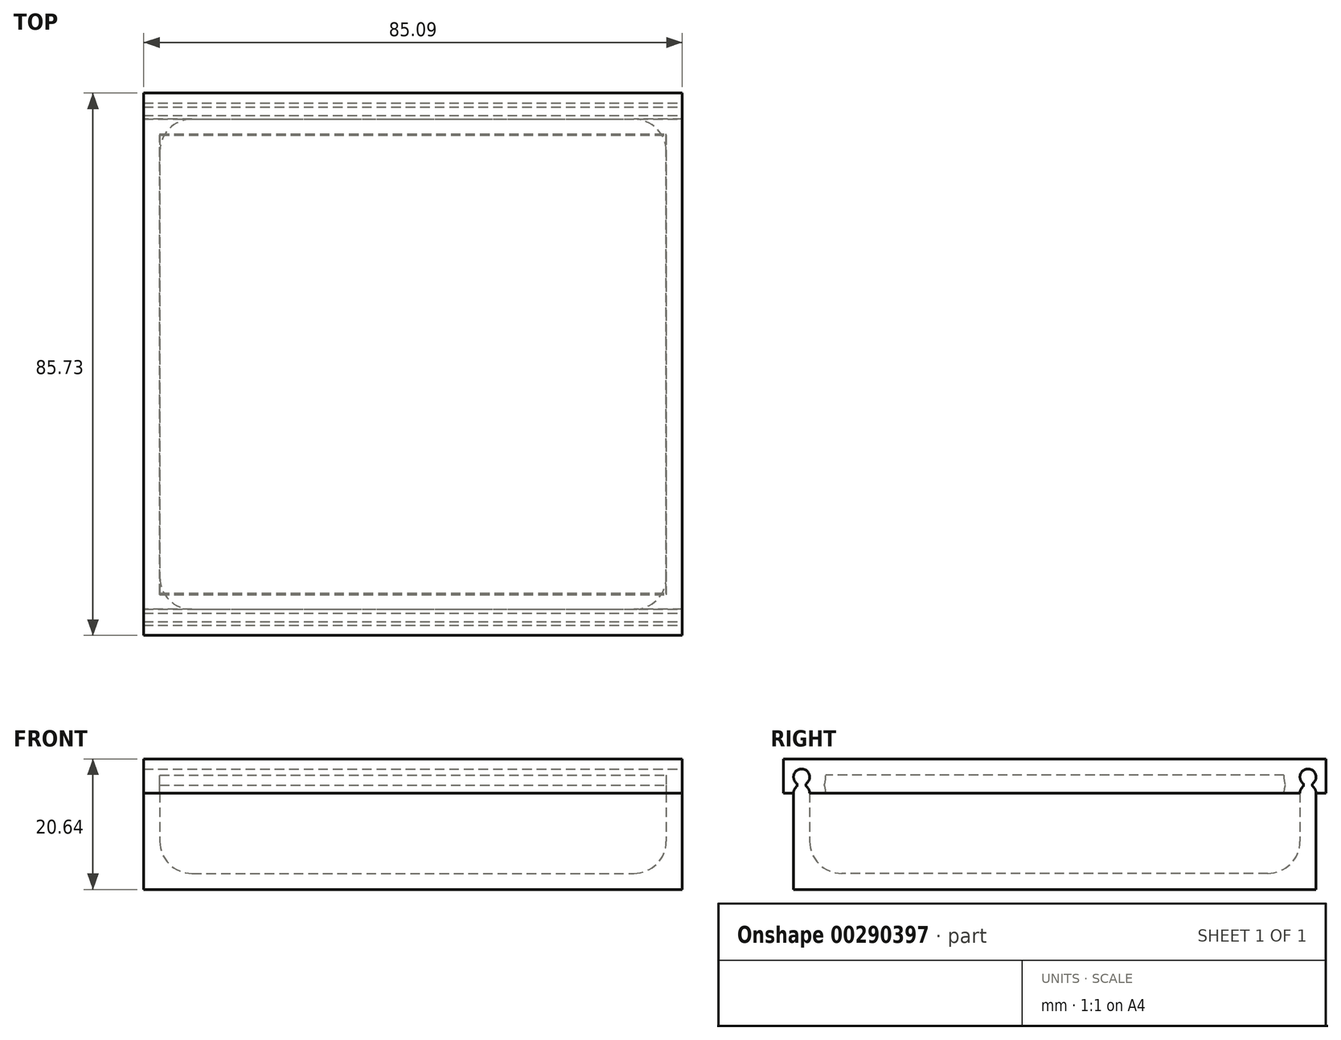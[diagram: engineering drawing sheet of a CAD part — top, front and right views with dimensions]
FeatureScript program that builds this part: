
annotation { "Feature Type Name" : "Feature", "Feature Type Description" : "" }
export const myFeature = defineFeature(function(context is Context, id is Id, definition is map)
    precondition{}
    {
        {
            var Q0;
            Q0=qCreatedBy(makeId("Top.planeOp"),FACE);
            var sketch = newSketch(context, id + "F0", { "sketchPlane" : qUnion([Q0])});
            skLineSegment(sketch, "E0.bottom", {"start": v(0, 82.55) * mm, "end": v(85.1, 82.55) * mm});
            skLineSegment(sketch, "E0.top", {"start": v(0, 0) * mm, "end": v(85.1, 0) * mm});
            skLineSegment(sketch, "E0.left", {"start": v(0, 82.55) * mm, "end": v(0, 0) * mm});
            skLineSegment(sketch, "E0.right", {"start": v(85.1, 82.55) * mm, "end": v(85.1, 0) * mm});
            skSolve(sketch);
        }
        {
            var Q0;
            Q0 = qSketchRegion(id + "F0", true);
            extrude(context, id + "F1", {"entities" : qUnion([Q0]), "depth" : 15.24 * mm, "offsetDistance" : 25.4 * mm});
        }
        {
            var Q0;
            Q0=makeQuery(id+"F1.opExtrude","CAP_FACE",FACE,{"disambiguationData":[OSD([sQuery(id+"F0.wireOp",EDGE,"E0.bottom"),sQuery(id+"F0.wireOp",EDGE,"E0.top"),sQuery(id+"F0.wireOp",EDGE,"E0.left"),sQuery(id+"F0.wireOp",EDGE,"E0.right")])],"isStart":false});
            shell(context, id + "F2", {"entities" : qUnion([Q0]), "thickness" : 2.54 * mm});
        }
        {
            var Q0;
            Q0=makeQuery(id+"F1.opExtrude","SWEPT_FACE",FACE,{"disambiguationData":[OSD([sQuery(id+"F0.wireOp",EDGE,"E0.left")])]});
            var sketch = newSketch(context, id + "F3", { "sketchPlane" : qUnion([Q0])});
            skLineSegment(sketch, "E1.bottom", {"start": v(0, 15.24) * mm, "end": v(-2.54, 15.24) * mm});
            skLineSegment(sketch, "E1.top", {"start": v(-1.27, 16.5) * mm, "end": v(-1.27, 16.5) * mm});
            skArc(sketch, "E2", {"start": v(-0.44, 16.81) * mm, "mid": v(-1.27, 19.05) * mm, "end": v(-2.1, 16.81) * mm});
            skPoint(sketch, "E2.centerSnap0", {"position": v(-1.27, 16.5) * mm});
            skPoint(sketch, "E3.visualSharp", {"position": v(-2.54, 16.5) * mm});
            skArc(sketch, "E3.filletArc", {"start": v(-2.1, 16.2) * mm, "mid": v(-2.42, 15.77) * mm, "end": v(-2.54, 15.24) * mm});
            skPoint(sketch, "E4.visualSharp", {"position": v(0, 16.5) * mm});
            skArc(sketch, "E4.filletArc", {"start": v(0, 15.24) * mm, "mid": v(-0.12, 15.77) * mm, "end": v(-0.44, 16.2) * mm});
            skArc(sketch, "E5", {"start": v(-2.1, 16.2) * mm, "mid": v(-1.95, 16.5) * mm, "end": v(-2.1, 16.81) * mm});
            skLineSegment(sketch, "E6", {"start": v(-1.27, 17.78) * mm, "end": v(-1.27, 16.5) * mm, "construction": true});
            skArc(sketch, "E7.MirrorCS", {"start": v(-0.44, 16.2) * mm, "mid": v(-0.59, 16.5) * mm, "end": v(-0.44, 16.81) * mm});
            skArc(sketch, "E8.MirrorCS", {"start": v(-0.44, 16.2) * mm, "mid": v(-0.12, 15.77) * mm, "end": v(0, 15.24) * mm});
            skLineSegment(sketch, "E9", {"start": v(-41.28, 15.24) * mm, "end": v(-41.28, 0) * mm, "construction": true});
            skArc(sketch, "E10.MirrorCS", {"start": v(-82.1, 16.2) * mm, "mid": v(-81.96, 16.5) * mm, "end": v(-82.1, 16.81) * mm});
            skArc(sketch, "E11.MirrorCS", {"start": v(-82.55, 15.24) * mm, "mid": v(-82.43, 15.77) * mm, "end": v(-82.1, 16.2) * mm});
            skArc(sketch, "E12.MirrorCS", {"start": v(-82.1, 16.2) * mm, "mid": v(-82.43, 15.77) * mm, "end": v(-82.55, 15.24) * mm});
            skArc(sketch, "E13.MirrorCS", {"start": v(-80.45, 16.2) * mm, "mid": v(-80.6, 16.5) * mm, "end": v(-80.45, 16.81) * mm});
            skLineSegment(sketch, "E14.MirrorCS", {"start": v(-82.55, 15.24) * mm, "end": v(-80.01, 15.24) * mm});
            skLineSegment(sketch, "E15.MirrorCS", {"start": v(-81.28, 17.78) * mm, "end": v(-81.28, 16.5) * mm, "construction": true});
            skArc(sketch, "E16.MirrorCS", {"start": v(-80.45, 16.2) * mm, "mid": v(-80.13, 15.77) * mm, "end": v(-80.01, 15.24) * mm});
            skPoint(sketch, "E17.MirrorP", {"position": v(-81.28, 16.5) * mm});
            skLineSegment(sketch, "E18.MirrorCS", {"start": v(-81.28, 16.5) * mm, "end": v(-81.28, 16.5) * mm});
            skPoint(sketch, "E19.MirrorP", {"position": v(-80.01, 16.5) * mm});
            skPoint(sketch, "E20.MirrorP", {"position": v(-82.55, 16.5) * mm});
            skArc(sketch, "E21.MirrorCS", {"start": v(-82.1, 16.81) * mm, "mid": v(-81.28, 19.05) * mm, "end": v(-80.45, 16.81) * mm});
            skSolve(sketch);
        }
        {
            var Q0;
            Q0 = qSketchRegion(id + "F3", true);
            var Q1;
            Q1=makeQuery(id+"F1.opExtrude","SWEPT_FACE",FACE,{"disambiguationData":[OSD([sQuery(id+"F0.wireOp",EDGE,"E0.right")])]});
            extrude(context, id + "F4", {"entities" : qUnion([Q0]), "operationType" : NewBodyOperationType.ADD, "endBound" : BoundingType.UP_TO_SURFACE, "oppositeDirection" : true, "depth" : 25.4 * mm, "endBoundEntityFace" : qUnion([Q1]), "offsetDistance" : 25.4 * mm});
        }
        {
            var Q0;
            Q0=qCreatedBy(makeId("Front.planeOp"),FACE);
            cPlane(context, id + "F5", {"entities" : qUnion([Q0]), "cplaneType" : CPlaneType.OFFSET, "offset" : 41.27 * mm, "oppositeDirection" : true, "width" : 152.4 * mm, "height" : 152.4 * mm});
        }
        {
            var Q0;
            {var subQ0=sQuery(id+"F0.wireOp",EDGE,"E0.right");Q0=makeQuery(id+"F4.boolean.opBoolean","MERGE",FACE,{"derivedFrom":[makeQuery(id+"F1.opExtrude","SWEPT_FACE",FACE,{"disambiguationData":[OSD([subQ0])]}),makeQuery(id+"F4.opExtrude","CAP_FACE",FACE,{"disambiguationData":[OSD([subQ0]),OD(0.0)],"isStart":false}),makeQuery(id+"F4.opExtrude","CAP_FACE",FACE,{"disambiguationData":[OSD([subQ0]),OD(1.0)],"isStart":false})]});}
            var sketch = newSketch(context, id + "F6", { "sketchPlane" : qUnion([Q0])});
            skLineSegment(sketch, "E22", {"start": v(2.54, 15.24) * mm, "end": v(-2.32, 15.24) * mm, "construction": true});
            skArc(sketch, "E23", {"start": v(2.54, 15.24) * mm, "mid": v(2.42, 15.77) * mm, "end": v(2.1, 16.2) * mm});
            skArc(sketch, "E24", {"start": v(2.1, 16.81) * mm, "mid": v(1.27, 19.05) * mm, "end": v(0.44, 16.81) * mm});
            skArc(sketch, "E25", {"start": v(2.1, 16.81) * mm, "mid": v(1.95, 16.5) * mm, "end": v(2.1, 16.2) * mm});
            skArc(sketch, "E26", {"start": v(0.44, 16.81) * mm, "mid": v(0.59, 16.5) * mm, "end": v(0.44, 16.2) * mm});
            skArc(sketch, "E27.trimOffspring", {"start": v(0.44, 16.2) * mm, "mid": v(0.12, 15.77) * mm, "end": v(0, 15.24) * mm});
            skLineSegment(sketch, "E28", {"start": v(0, 15.24) * mm, "end": v(-1.59, 15.24) * mm});
            skLineSegment(sketch, "E29", {"start": v(-1.59, 15.24) * mm, "end": v(-1.59, 20.64) * mm});
            skLineSegment(sketch, "E30", {"start": v(1.27, 19.05) * mm, "end": v(-1.87, 19.05) * mm, "construction": true});
            skArc(sketch, "E31.MirrorCS", {"start": v(82.1, 16.81) * mm, "mid": v(81.96, 16.5) * mm, "end": v(82.1, 16.2) * mm});
            skArc(sketch, "E32.MirrorCS", {"start": v(82.1, 16.2) * mm, "mid": v(82.43, 15.77) * mm, "end": v(82.55, 15.24) * mm});
            skLineSegment(sketch, "E33.MirrorCS", {"start": v(82.55, 15.24) * mm, "end": v(84.14, 15.24) * mm});
            skArc(sketch, "E34.MirrorCS", {"start": v(80.01, 15.24) * mm, "mid": v(80.13, 15.77) * mm, "end": v(80.45, 16.2) * mm});
            skLineSegment(sketch, "E35.MirrorCS", {"start": v(80.01, 15.24) * mm, "end": v(84.87, 15.24) * mm, "construction": true});
            skArc(sketch, "E36.MirrorCS", {"start": v(80.45, 16.81) * mm, "mid": v(80.6, 16.5) * mm, "end": v(80.45, 16.2) * mm});
            skLineSegment(sketch, "E37.MirrorCS", {"start": v(81.28, 19.05) * mm, "end": v(84.42, 19.05) * mm, "construction": true});
            skArc(sketch, "E38.MirrorCS", {"start": v(80.45, 16.81) * mm, "mid": v(81.28, 19.05) * mm, "end": v(82.1, 16.81) * mm});
            skLineSegment(sketch, "E39.MirrorCS", {"start": v(84.14, 15.24) * mm, "end": v(84.14, 20.64) * mm});
            skLineSegment(sketch, "E40", {"start": v(-1.59, 20.64) * mm, "end": v(84.14, 20.64) * mm});
            skLineSegment(sketch, "E41", {"start": v(80.01, 15.24) * mm, "end": v(2.54, 15.24) * mm});
            skSolve(sketch);
        }
        {
            var Q0;
            Q0 = qSketchRegion(id + "F6", true);
            var Q1;
            Q1=makeQuery(id+"F4.boolean.opBoolean","MERGE",FACE,{"derivedFrom":[makeQuery(id+"F1.opExtrude","SWEPT_FACE",FACE,{"disambiguationData":[OSD([sQuery(id+"F0.wireOp",EDGE,"E0.left")])]}),makeQuery(id+"F4.opExtrude","CAP_FACE",FACE,{"disambiguationData":[OSD([sQuery(id+"F3.wireOp",EDGE,"E1.bottom"),sQuery(id+"F3.wireOp",EDGE,"E2"),sQuery(id+"F3.wireOp",EDGE,"E3.filletArc"),sQuery(id+"F3.wireOp",EDGE,"E5"),sQuery(id+"F3.wireOp",EDGE,"E7.MirrorCS"),sQuery(id+"F3.wireOp",EDGE,"E8.MirrorCS")])],"isStart":true}),makeQuery(id+"F4.opExtrude","CAP_FACE",FACE,{"disambiguationData":[OSD([sQuery(id+"F3.wireOp",EDGE,"E10.MirrorCS"),sQuery(id+"F3.wireOp",EDGE,"E12.MirrorCS"),sQuery(id+"F3.wireOp",EDGE,"E13.MirrorCS"),sQuery(id+"F3.wireOp",EDGE,"E14.MirrorCS"),sQuery(id+"F3.wireOp",EDGE,"E16.MirrorCS"),sQuery(id+"F3.wireOp",EDGE,"E21.MirrorCS")])],"isStart":true})]});
            extrude(context, id + "F7", {"entities" : qUnion([Q0]), "endBound" : BoundingType.UP_TO_SURFACE, "oppositeDirection" : true, "depth" : 25.4 * mm, "endBoundEntityFace" : qUnion([Q1]), "offsetDistance" : 25.4 * mm});
        }
        {
            var Q0;
            Q0=makeQuery(id+"F7.opExtrude","SWEPT_FACE",FACE,{"disambiguationData":[OSD([sQuery(id+"F6.wireOp",EDGE,"E41")])]});
            shell(context, id + "F8", {"entities" : qUnion([Q0]), "thickness" : 2.54 * mm});
        }
        {
            var Q0;
            Q0=makeQuery(id+"F2.opShell","OFFSET_EDGE",EDGE,{"disambiguationData":[OSD([sQuery(id+"F0.wireOp",EDGE,"E0.bottom"),sQuery(id+"F0.wireOp",EDGE,"E0.left")])]});
            var Q1;
            Q1=makeQuery(id+"F2.opShell","OFFSET_FACE",FACE,{"disambiguationData":[OSD([sQuery(id+"F0.wireOp",EDGE,"E0.bottom"),sQuery(id+"F0.wireOp",EDGE,"E0.top"),sQuery(id+"F0.wireOp",EDGE,"E0.left"),sQuery(id+"F0.wireOp",EDGE,"E0.right")])]});
            var Q2;
            Q2=makeQuery(id+"F2.opShell","OFFSET_EDGE",EDGE,{"disambiguationData":[OSD([sQuery(id+"F0.wireOp",EDGE,"E0.top"),sQuery(id+"F0.wireOp",EDGE,"E0.left")])]});
            var Q3;
            Q3=makeQuery(id+"F2.opShell","OFFSET_EDGE",EDGE,{"disambiguationData":[OSD([sQuery(id+"F0.wireOp",EDGE,"E0.top"),sQuery(id+"F0.wireOp",EDGE,"E0.right")])]});
            var Q4;
            Q4=makeQuery(id+"F2.opShell","OFFSET_EDGE",EDGE,{"disambiguationData":[OSD([sQuery(id+"F0.wireOp",EDGE,"E0.bottom"),sQuery(id+"F0.wireOp",EDGE,"E0.right")])]});
            fillet(context, id + "F9", {"entities" : qUnion([Q0, Q1, Q2, Q3, Q4]), "radius" : 5.08 * mm, "tangentPropagation" : true, "allowEdgeOverflow" : false});
        }
    });
